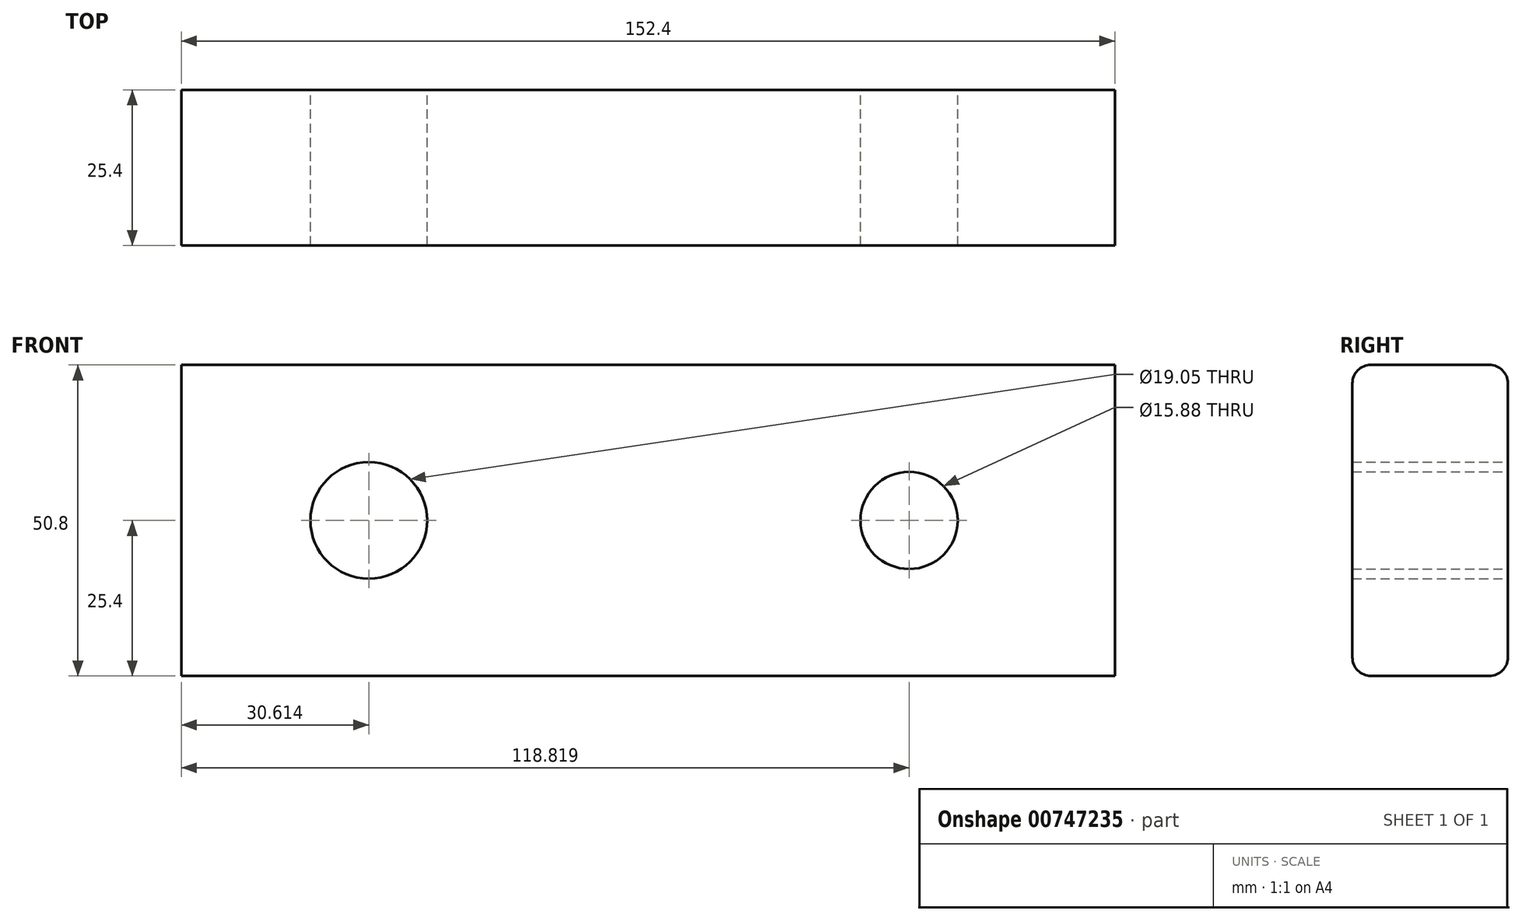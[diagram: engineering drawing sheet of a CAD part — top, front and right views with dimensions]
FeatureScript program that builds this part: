
annotation { "Feature Type Name" : "Feature", "Feature Type Description" : "" }
export const myFeature = defineFeature(function(context is Context, id is Id, definition is map)
    precondition{}
    {
        {
            var Q0;
            Q0=qCreatedBy(makeId("Front.planeOp"),FACE);
            var sketch = newSketch(context, id + "F0", { "sketchPlane" : qUnion([Q0])});
            skLineSegment(sketch, "E0.bottom", {"start": v(-76.2, -25.4) * mm, "end": v(76.2, -25.4) * mm});
            skLineSegment(sketch, "E0.top", {"start": v(-76.2, 25.4) * mm, "end": v(76.2, 25.4) * mm});
            skLineSegment(sketch, "E0.left", {"start": v(-76.2, -25.4) * mm, "end": v(-76.2, 25.4) * mm});
            skLineSegment(sketch, "E0.right", {"start": v(76.2, -25.4) * mm, "end": v(76.2, 25.4) * mm});
            skPoint(sketch, "E0.middle", {"position": v(0, 0) * mm});
            skCircle(sketch, "E1", {"center": v(-45.59, 0) * mm, "radius": 9.53 * mm});
            skCircle(sketch, "E2", {"center": v(42.62, 0) * mm, "radius": 7.94 * mm});
            skSolve(sketch);
        }
        {
            var Q0;
            Q0=makeQuery(id+"F0.imprint","IMPRINT",FACE,{"disambiguationData":[TD([[makeQuery(id+"F0.imprint","IMPRINT",EDGE,{"derivedFrom":sQuery(id+"F0.wireOp",EDGE,"E0.bottom")}),1.0]])]});
            extrude(context, id + "F1", {"entities" : qUnion([Q0]), "depth" : 25.4 * mm, "offsetDistance" : 25.4 * mm});
        }
        {
            var Q0;
            Q0=makeQuery(id+"F1.opExtrude","CAP_EDGE",EDGE,{"disambiguationData":[OSD([sQuery(id+"F0.wireOp",EDGE,"E0.top")])],"isStart":false});
            var Q1;
            Q1=makeQuery(id+"F1.opExtrude","CAP_EDGE",EDGE,{"disambiguationData":[OSD([sQuery(id+"F0.wireOp",EDGE,"E0.bottom")])],"isStart":false});
            var Q2;
            Q2=makeQuery(id+"F1.opExtrude","CAP_EDGE",EDGE,{"disambiguationData":[OSD([sQuery(id+"F0.wireOp",EDGE,"E0.top")])],"isStart":true});
            var Q3;
            Q3=makeQuery(id+"F1.opExtrude","CAP_EDGE",EDGE,{"disambiguationData":[OSD([sQuery(id+"F0.wireOp",EDGE,"E0.bottom")])],"isStart":true});
            fillet(context, id + "F2", {"entities" : qUnion([Q0, Q1, Q2, Q3]), "radius" : 3.05 * mm, "tangentPropagation" : true, "allowEdgeOverflow" : false});
        }
    });
